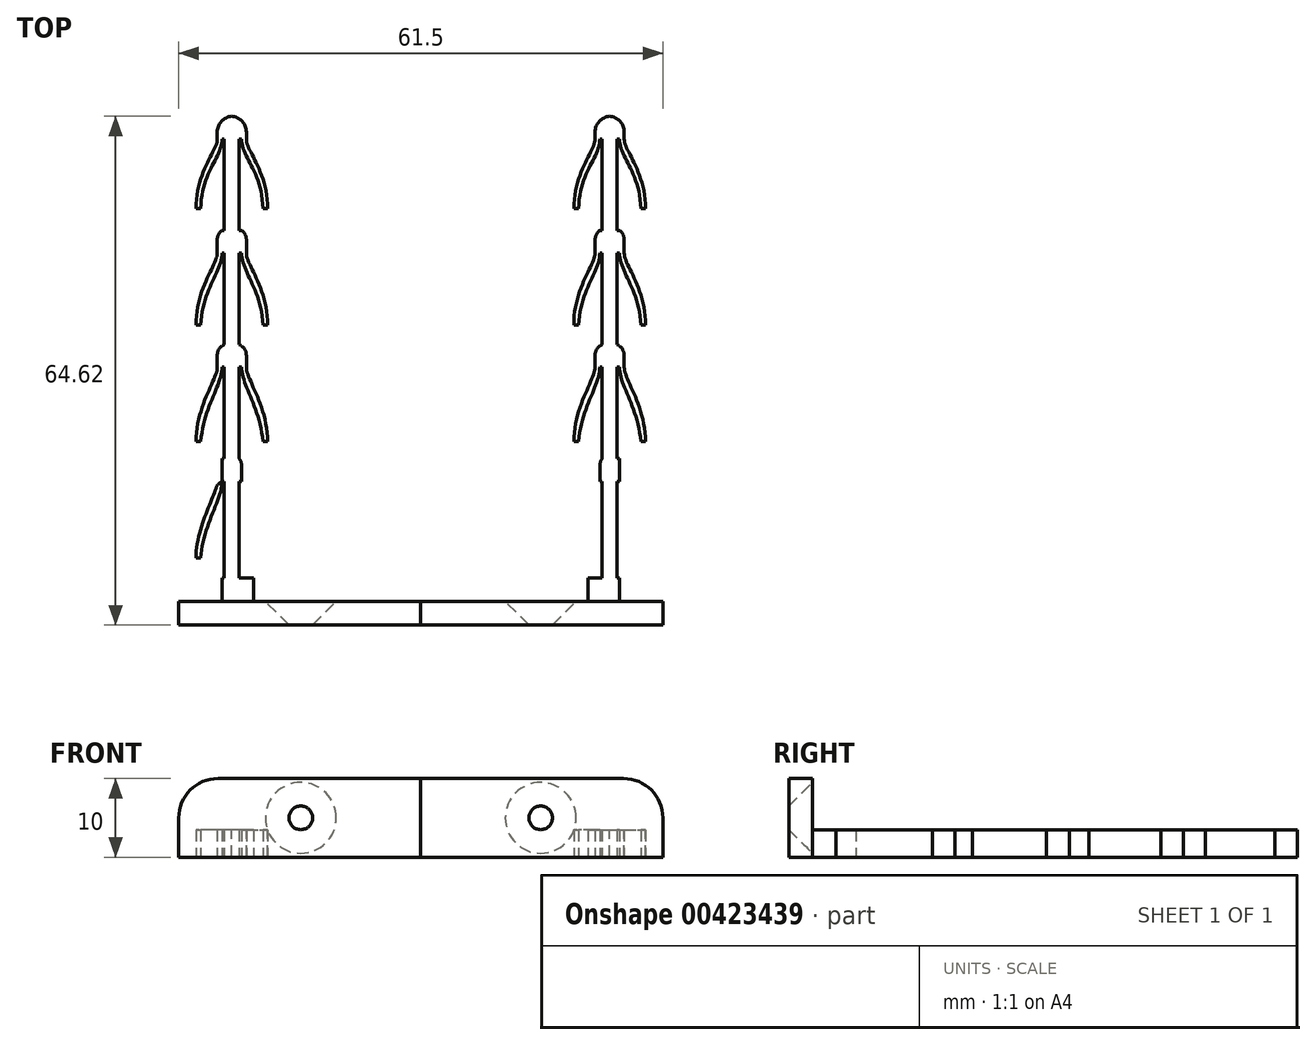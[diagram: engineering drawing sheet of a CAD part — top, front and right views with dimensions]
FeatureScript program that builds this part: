
annotation { "Feature Type Name" : "Feature", "Feature Type Description" : "" }
export const myFeature = defineFeature(function(context is Context, id is Id, definition is map)
    precondition{}
    {
        {
            var Q0;
            Q0=qCreatedBy(makeId("Top.planeOp"),FACE);
            var sketch = newSketch(context, id + "F0", { "sketchPlane" : qUnion([Q0])});
            skLineSegment(sketch, "E0.bottom", {"start": v(0, 0) * mm, "end": v(-15.51, 0) * mm});
            skLineSegment(sketch, "E0.top", {"start": v(0, 3) * mm, "end": v(-15.51, 3) * mm});
            skLineSegment(sketch, "E0.left", {"start": v(0, 0) * mm, "end": v(0, 3) * mm});
            skLineSegment(sketch, "E0.right", {"start": v(-15.51, 0) * mm, "end": v(-15.51, 3) * mm});
            skLineSegment(sketch, "E1.bottom", {"start": v(-10.01, 3) * mm, "end": v(-8.76, 3.02) * mm});
            skLineSegment(sketch, "E1.left", {"start": v(-10.01, 3) * mm, "end": v(-10.01, 18.24) * mm});
            skLineSegment(sketch, "E1.right", {"start": v(-8.76, 3.02) * mm, "end": v(-8.76, 64.62) * mm});
            skLineSegment(sketch, "E2.bottom", {"start": v(-10.01, 3) * mm, "end": v(-11.51, 3) * mm});
            skLineSegment(sketch, "E2.top", {"start": v(-10.01, 6) * mm, "end": v(-11.51, 6) * mm});
            skLineSegment(sketch, "E2.left", {"start": v(-10.01, 3) * mm, "end": v(-10.01, 6) * mm});
            skLineSegment(sketch, "E2.right", {"start": v(-11.51, 3) * mm, "end": v(-11.51, 6) * mm});
            skLineSegment(sketch, "E3.top", {"start": v(-10.01, 18.24) * mm, "end": v(-10.61, 18.24) * mm});
            skLineSegment(sketch, "E4", {"start": v(-13.31, 8.5) * mm, "end": v(-12.71, 8.5) * mm});
            skFitSpline(sketch, "E5", {"points": [v(-10.01, 18.24) * mm, v(-12.71, 8.5) * mm], "startDerivative": vector(0, -7.07) * mm, "endDerivative": vector(-0.68, -12.06) * mm});
            skFitSpline(sketch, "E6", {"points": [v(-10.61, 18.24) * mm, v(-13.31, 8.5) * mm], "startDerivative": vector(0.14, -4.37) * mm, "endDerivative": vector(0.03, -12.59) * mm});
            skLineSegment(sketch, "E7.bottom", {"start": v(-10.61, 18.24) * mm, "end": v(-10.01, 18.24) * mm});
            skLineSegment(sketch, "E7.top", {"start": v(-10.61, 21.13) * mm, "end": v(-10.01, 21.13) * mm});
            skLineSegment(sketch, "E7.left", {"start": v(-10.61, 18.24) * mm, "end": v(-10.61, 21.13) * mm});
            skLineSegment(sketch, "E7.right", {"start": v(-10.01, 18.24) * mm, "end": v(-10.01, 21.13) * mm});
            skLineSegment(sketch, "E8", {"start": v(-10.01, 21.13) * mm, "end": v(-10.01, 64.62) * mm});
            skLineSegment(sketch, "E9", {"start": v(-10.01, 64.62) * mm, "end": v(-8.76, 64.62) * mm});
            skFitSpline(sketch, "E10", {"points": [v(-10.01, 32.74) * mm, v(-12.71, 23.3) * mm], "startDerivative": vector(0, -7.07) * mm, "endDerivative": vector(-1.2, -13.71) * mm});
            skFitSpline(sketch, "E11", {"points": [v(-10.61, 32.74) * mm, v(-13.31, 23.3) * mm], "startDerivative": vector(0.14, -4.37) * mm, "endDerivative": vector(-0.1, -13.84) * mm});
            skLineSegment(sketch, "E12.bottom", {"start": v(-10.61, 32.74) * mm, "end": v(-10.01, 32.74) * mm});
            skLineSegment(sketch, "E12.left", {"start": v(-10.61, 32.74) * mm, "end": v(-10.61, 35.63) * mm});
            skLineSegment(sketch, "E13", {"start": v(-13.31, 23.3) * mm, "end": v(-12.71, 23.3) * mm});
            skLineSegment(sketch, "E14.top", {"start": v(-10.61, 35.63) * mm, "end": v(-10.01, 35.63) * mm});
            skFitSpline(sketch, "E15", {"points": [v(-10.01, 47.24) * mm, v(-12.71, 38.1) * mm], "startDerivative": vector(0, -7.07) * mm, "endDerivative": vector(-0.68, -13.91) * mm});
            skFitSpline(sketch, "E16", {"points": [v(-10.61, 47.24) * mm, v(-13.31, 38.1) * mm], "startDerivative": vector(0.14, -4.37) * mm, "endDerivative": vector(0.16, -14.04) * mm});
            skLineSegment(sketch, "E17.bottom", {"start": v(-10.61, 47.24) * mm, "end": v(-10.01, 47.24) * mm});
            skLineSegment(sketch, "E17.left", {"start": v(-10.61, 47.24) * mm, "end": v(-10.61, 50.13) * mm});
            skLineSegment(sketch, "E18", {"start": v(-13.31, 38.1) * mm, "end": v(-12.71, 38.1) * mm});
            skLineSegment(sketch, "E19.top", {"start": v(-10.61, 50.13) * mm, "end": v(-10.01, 50.13) * mm});
            skFitSpline(sketch, "E20", {"points": [v(-10.01, 61.74) * mm, v(-12.71, 52.9) * mm], "startDerivative": vector(0, -7.07) * mm, "endDerivative": vector(-0.28, -14.05) * mm});
            skFitSpline(sketch, "E21", {"points": [v(-10.61, 61.74) * mm, v(-13.31, 52.9) * mm], "startDerivative": vector(0.14, -4.37) * mm, "endDerivative": vector(0.02, -14.1) * mm});
            skLineSegment(sketch, "E22.bottom", {"start": v(-10.61, 61.74) * mm, "end": v(-10.01, 61.74) * mm});
            skLineSegment(sketch, "E22.left", {"start": v(-10.61, 61.74) * mm, "end": v(-10.61, 64.62) * mm});
            skLineSegment(sketch, "E23", {"start": v(-13.31, 52.9) * mm, "end": v(-12.71, 52.9) * mm});
            skLineSegment(sketch, "E24", {"start": v(-10.61, 64.62) * mm, "end": v(-10.01, 64.62) * mm});
            skLineSegment(sketch, "E25.MirrorCS", {"start": v(-6.91, 18.24) * mm, "end": v(-7.51, 18.24) * mm});
            skLineSegment(sketch, "E26.MirrorCS", {"start": v(-7.51, 18.24) * mm, "end": v(-6.91, 18.24) * mm});
            skLineSegment(sketch, "E27.MirrorCS", {"start": v(-6.91, 32.74) * mm, "end": v(-7.51, 32.74) * mm});
            skLineSegment(sketch, "E28.MirrorCS", {"start": v(-6.91, 47.24) * mm, "end": v(-7.51, 47.24) * mm});
            skLineSegment(sketch, "E29.MirrorCS", {"start": v(-7.51, 6) * mm, "end": v(-6.01, 6) * mm});
            skLineSegment(sketch, "E30.MirrorCS", {"start": v(-6.91, 61.74) * mm, "end": v(-7.51, 61.74) * mm});
            skLineSegment(sketch, "E31.MirrorCS", {"start": v(-6.91, 61.74) * mm, "end": v(-6.91, 64.62) * mm});
            skLineSegment(sketch, "E32.MirrorCS", {"start": v(-6.91, 64.62) * mm, "end": v(-7.51, 64.62) * mm});
            skLineSegment(sketch, "E33.MirrorCS", {"start": v(-4.21, 52.9) * mm, "end": v(-4.81, 52.9) * mm});
            skLineSegment(sketch, "E34.MirrorCS", {"start": v(-4.21, 38.1) * mm, "end": v(-4.81, 38.1) * mm});
            skLineSegment(sketch, "E35.MirrorCS", {"start": v(-4.21, 8.5) * mm, "end": v(-4.81, 8.5) * mm});
            skLineSegment(sketch, "E36.MirrorCS", {"start": v(-6.91, 18.24) * mm, "end": v(-6.91, 21.13) * mm});
            skLineSegment(sketch, "E37.MirrorCS", {"start": v(-4.21, 23.3) * mm, "end": v(-4.81, 23.3) * mm});
            skLineSegment(sketch, "E38.MirrorCS", {"start": v(-7.51, 18.24) * mm, "end": v(-7.51, 21.13) * mm});
            skLineSegment(sketch, "E39.MirrorCS", {"start": v(-6.91, 21.13) * mm, "end": v(-7.51, 21.13) * mm});
            skLineSegment(sketch, "E40.MirrorCS", {"start": v(-6.91, 50.13) * mm, "end": v(-7.51, 50.13) * mm});
            skLineSegment(sketch, "E41.MirrorCS", {"start": v(-6.91, 47.24) * mm, "end": v(-6.91, 50.13) * mm});
            skLineSegment(sketch, "E42.MirrorCS", {"start": v(-6.91, 32.74) * mm, "end": v(-6.91, 35.63) * mm});
            skLineSegment(sketch, "E43.MirrorCS", {"start": v(-6.91, 35.63) * mm, "end": v(-7.51, 35.63) * mm});
            skFitSpline(sketch, "E44.MirrorCS", {"points": [v(-6.91, 61.74) * mm, v(-4.21, 52.9) * mm], "startDerivative": vector(-0.14, -4.37) * mm, "endDerivative": vector(-0.02, -14.1) * mm});
            skLineSegment(sketch, "E45.MirrorCS", {"start": v(-7.51, 21.13) * mm, "end": v(-7.51, 64.62) * mm});
            skFitSpline(sketch, "E46.MirrorCS", {"points": [v(-7.51, 18.24) * mm, v(-4.81, 8.5) * mm], "startDerivative": vector(0, -7.07) * mm, "endDerivative": vector(0.68, -12.06) * mm});
            skFitSpline(sketch, "E47.MirrorCS", {"points": [v(-7.51, 32.74) * mm, v(-4.81, 23.3) * mm], "startDerivative": vector(0, -7.07) * mm, "endDerivative": vector(1.2, -13.71) * mm});
            skFitSpline(sketch, "E48.MirrorCS", {"points": [v(-7.51, 47.24) * mm, v(-4.81, 38.1) * mm], "startDerivative": vector(0, -7.07) * mm, "endDerivative": vector(0.68, -13.91) * mm});
            skFitSpline(sketch, "E49.MirrorCS", {"points": [v(-6.91, 32.74) * mm, v(-4.21, 23.3) * mm], "startDerivative": vector(-0.14, -4.37) * mm, "endDerivative": vector(0.1, -13.84) * mm});
            skFitSpline(sketch, "E50.MirrorCS", {"points": [v(-7.51, 61.74) * mm, v(-4.81, 52.9) * mm], "startDerivative": vector(0, -7.07) * mm, "endDerivative": vector(0.28, -14.05) * mm});
            skFitSpline(sketch, "E51.MirrorCS", {"points": [v(-6.91, 18.24) * mm, v(-4.21, 8.5) * mm], "startDerivative": vector(-0.14, -4.37) * mm, "endDerivative": vector(-0.03, -12.59) * mm});
            skFitSpline(sketch, "E52.MirrorCS", {"points": [v(-6.91, 47.24) * mm, v(-4.21, 38.1) * mm], "startDerivative": vector(-0.14, -4.37) * mm, "endDerivative": vector(-0.16, -14.04) * mm});
            skLineSegment(sketch, "E53.MirrorCS", {"start": v(-7.51, 64.62) * mm, "end": v(-8.76, 64.62) * mm});
            skLineSegment(sketch, "E54.MirrorCS", {"start": v(-7.51, 3) * mm, "end": v(-7.51, 18.24) * mm});
            skLineSegment(sketch, "E55.MirrorCS", {"start": v(-6.01, 3) * mm, "end": v(-6.01, 6) * mm});
            skLineSegment(sketch, "E56.bottom", {"start": v(0, 3) * mm, "end": v(15.24, 3) * mm});
            skLineSegment(sketch, "E56.top", {"start": v(0, 0) * mm, "end": v(15.24, 0) * mm});
            skLineSegment(sketch, "E56.left", {"start": v(0, 3) * mm, "end": v(0, 0) * mm});
            skLineSegment(sketch, "E56.right", {"start": v(15.24, 3) * mm, "end": v(15.24, 0) * mm});
            skLineSegment(sketch, "E57.bottom", {"start": v(-10.01, 61.74) * mm, "end": v(-9.71, 61.74) * mm});
            skLineSegment(sketch, "E57.top", {"start": v(-10.01, 50.13) * mm, "end": v(-9.71, 50.13) * mm});
            skLineSegment(sketch, "E57.left", {"start": v(-10.01, 61.74) * mm, "end": v(-10.01, 50.13) * mm});
            skLineSegment(sketch, "E57.right", {"start": v(-9.71, 61.74) * mm, "end": v(-9.71, 50.13) * mm});
            skLineSegment(sketch, "E58.bottom", {"start": v(-10.01, 47.24) * mm, "end": v(-9.71, 47.24) * mm});
            skLineSegment(sketch, "E58.top", {"start": v(-10.01, 35.63) * mm, "end": v(-9.71, 35.63) * mm});
            skLineSegment(sketch, "E58.left", {"start": v(-10.01, 47.24) * mm, "end": v(-10.01, 35.63) * mm});
            skLineSegment(sketch, "E58.right", {"start": v(-9.71, 47.24) * mm, "end": v(-9.71, 35.63) * mm});
            skLineSegment(sketch, "E59.bottom", {"start": v(-10.01, 32.74) * mm, "end": v(-9.71, 32.74) * mm});
            skLineSegment(sketch, "E59.top", {"start": v(-10.01, 21.13) * mm, "end": v(-9.71, 21.13) * mm});
            skLineSegment(sketch, "E59.left", {"start": v(-10.01, 32.74) * mm, "end": v(-10.01, 21.13) * mm});
            skLineSegment(sketch, "E59.right", {"start": v(-9.71, 32.74) * mm, "end": v(-9.71, 21.13) * mm});
            skLineSegment(sketch, "E60.bottom", {"start": v(-10.01, 18.24) * mm, "end": v(-9.71, 18.24) * mm});
            skLineSegment(sketch, "E60.top", {"start": v(-10.01, 6) * mm, "end": v(-9.71, 6) * mm});
            skLineSegment(sketch, "E60.left", {"start": v(-10.01, 18.24) * mm, "end": v(-10.01, 6) * mm});
            skLineSegment(sketch, "E60.right", {"start": v(-9.71, 18.24) * mm, "end": v(-9.71, 6) * mm});
            skLineSegment(sketch, "E61.MirrorCS", {"start": v(-7.51, 61.74) * mm, "end": v(-7.81, 61.74) * mm});
            skLineSegment(sketch, "E62.MirrorCS", {"start": v(-7.81, 61.74) * mm, "end": v(-7.81, 50.13) * mm});
            skLineSegment(sketch, "E63.MirrorCS", {"start": v(-7.51, 50.13) * mm, "end": v(-7.81, 50.13) * mm});
            skLineSegment(sketch, "E64.MirrorCS", {"start": v(-7.51, 47.24) * mm, "end": v(-7.81, 47.24) * mm});
            skLineSegment(sketch, "E65.MirrorCS", {"start": v(-7.81, 47.24) * mm, "end": v(-7.81, 35.63) * mm});
            skLineSegment(sketch, "E66.MirrorCS", {"start": v(-7.51, 35.63) * mm, "end": v(-7.81, 35.63) * mm});
            skLineSegment(sketch, "E67.MirrorCS", {"start": v(-7.51, 32.74) * mm, "end": v(-7.81, 32.74) * mm});
            skLineSegment(sketch, "E68.MirrorCS", {"start": v(-7.81, 32.74) * mm, "end": v(-7.81, 21.13) * mm});
            skLineSegment(sketch, "E69.MirrorCS", {"start": v(-7.51, 21.13) * mm, "end": v(-7.81, 21.13) * mm});
            skLineSegment(sketch, "E70.MirrorCS", {"start": v(-7.51, 18.24) * mm, "end": v(-7.81, 18.24) * mm});
            skLineSegment(sketch, "E71.MirrorCS", {"start": v(-7.81, 18.24) * mm, "end": v(-7.81, 6) * mm});
            skLineSegment(sketch, "E72.MirrorCS", {"start": v(-7.51, 6) * mm, "end": v(-7.81, 6) * mm});
            skSolve(sketch);
        }
        {
            var Q0;
            {var subQ8=sQuery(id+"F0.wireOp",EDGE,"E1.bottom");Q0=makeQuery(id+"F0.imprint","IMPRINT",FACE,{"disambiguationData":[TD([[makeQuery(id+"F0.imprint","IMPRINT",EDGE,{"derivedFrom":subQ8}),-1.0]])]});}
            var Q1;
            Q1=makeQuery(id+"F0.imprint","IMPRINT",FACE,{"disambiguationData":[TD([[makeQuery(id+"F0.imprint","IMPRINT",EDGE,{"derivedFrom":sQuery(id+"F0.wireOp",EDGE,"E1.bottom")}),1.0]])]});
            var Q2;
            {var subQ2=sQuery(id+"F0.wireOp",EDGE,"E22.bottom");Q2=makeQuery(id+"F0.imprint","IMPRINT",FACE,{"disambiguationData":[TD([[makeQuery(id+"F0.imprint","IMPRINT",EDGE,{"derivedFrom":subQ2}),1.0]])]});}
            var Q3;
            {var subQ0=sQuery(id+"F0.wireOp",EDGE,"E30.MirrorCS");Q3=makeQuery(id+"F0.imprint","IMPRINT",FACE,{"disambiguationData":[TD([[makeQuery(id+"F0.imprint","IMPRINT",EDGE,{"derivedFrom":subQ0}),-1.0]])]});}
            var Q4;
            Q4=makeQuery(id+"F0.imprint","IMPRINT",FACE,{"disambiguationData":[TD([[makeQuery(id+"F0.imprint","IMPRINT",EDGE,{"derivedFrom":sQuery(id+"F0.wireOp",EDGE,"E30.MirrorCS")}),1.0]])]});
            var Q5;
            Q5=makeQuery(id+"F0.imprint","IMPRINT",FACE,{"disambiguationData":[TD([[makeQuery(id+"F0.imprint","IMPRINT",EDGE,{"derivedFrom":sQuery(id+"F0.wireOp",EDGE,"E20")}),-1.0]])]});
            var Q6;
            {var subQ0=sQuery(id+"F0.wireOp",EDGE,"E17.bottom");Q6=makeQuery(id+"F0.imprint","IMPRINT",FACE,{"disambiguationData":[TD([[makeQuery(id+"F0.imprint","IMPRINT",EDGE,{"derivedFrom":subQ0}),1.0]])]});}
            var Q7;
            {var subQ0=sQuery(id+"F0.wireOp",EDGE,"E28.MirrorCS");Q7=makeQuery(id+"F0.imprint","IMPRINT",FACE,{"disambiguationData":[TD([[makeQuery(id+"F0.imprint","IMPRINT",EDGE,{"derivedFrom":subQ0}),-1.0]])]});}
            var Q8;
            Q8=makeQuery(id+"F0.imprint","IMPRINT",FACE,{"disambiguationData":[TD([[makeQuery(id+"F0.imprint","IMPRINT",EDGE,{"derivedFrom":sQuery(id+"F0.wireOp",EDGE,"E28.MirrorCS")}),1.0]])]});
            var Q9;
            Q9=makeQuery(id+"F0.imprint","IMPRINT",FACE,{"disambiguationData":[TD([[makeQuery(id+"F0.imprint","IMPRINT",EDGE,{"derivedFrom":sQuery(id+"F0.wireOp",EDGE,"E15")}),-1.0]])]});
            var Q10;
            {var subQ0=sQuery(id+"F0.wireOp",EDGE,"E12.bottom");Q10=makeQuery(id+"F0.imprint","IMPRINT",FACE,{"disambiguationData":[TD([[makeQuery(id+"F0.imprint","IMPRINT",EDGE,{"derivedFrom":subQ0}),1.0]])]});}
            var Q11;
            {var subQ0=sQuery(id+"F0.wireOp",EDGE,"E27.MirrorCS");Q11=makeQuery(id+"F0.imprint","IMPRINT",FACE,{"disambiguationData":[TD([[makeQuery(id+"F0.imprint","IMPRINT",EDGE,{"derivedFrom":subQ0}),-1.0]])]});}
            var Q12;
            Q12=makeQuery(id+"F0.imprint","IMPRINT",FACE,{"disambiguationData":[TD([[makeQuery(id+"F0.imprint","IMPRINT",EDGE,{"derivedFrom":sQuery(id+"F0.wireOp",EDGE,"E27.MirrorCS")}),1.0]])]});
            var Q13;
            Q13=makeQuery(id+"F0.imprint","IMPRINT",FACE,{"disambiguationData":[TD([[makeQuery(id+"F0.imprint","IMPRINT",EDGE,{"derivedFrom":sQuery(id+"F0.wireOp",EDGE,"E10")}),-1.0]])]});
            var Q14;
            Q14=makeQuery(id+"F0.imprint","IMPRINT",FACE,{"disambiguationData":[TD([[makeQuery(id+"F0.imprint","IMPRINT",EDGE,{"derivedFrom":sQuery(id+"F0.wireOp",EDGE,"E26.MirrorCS")}),1.0]])]});
            var Q15;
            Q15=makeQuery(id+"F0.imprint","IMPRINT",FACE,{"disambiguationData":[TD([[makeQuery(id+"F0.imprint","IMPRINT",EDGE,{"derivedFrom":sQuery(id+"F0.wireOp",EDGE,"E7.bottom")}),1.0]])]});
            var Q16;
            Q16=makeQuery(id+"F0.imprint","IMPRINT",FACE,{"disambiguationData":[TD([[makeQuery(id+"F0.imprint","IMPRINT",EDGE,{"derivedFrom":sQuery(id+"F0.wireOp",EDGE,"E4")}),1.0]])]});
            var Q17;
            Q17=makeQuery(id+"F0.imprint","IMPRINT",FACE,{"disambiguationData":[TD([[makeQuery(id+"F0.imprint","IMPRINT",EDGE,{"derivedFrom":sQuery(id+"F0.wireOp",EDGE,"E26.MirrorCS")}),-1.0]])]});
            var Q18;
            {var subQ4=sQuery(id+"F0.wireOp",EDGE,"E29.MirrorCS");Q18=makeQuery(id+"F0.imprint","IMPRINT",FACE,{"disambiguationData":[TD([[makeQuery(id+"F0.imprint","IMPRINT",EDGE,{"derivedFrom":subQ4}),-1.0]])]});}
            var Q19;
            Q19=makeQuery(id+"F0.imprint","IMPRINT",FACE,{"disambiguationData":[TD([[makeQuery(id+"F0.imprint","IMPRINT",EDGE,{"derivedFrom":sQuery(id+"F0.wireOp",EDGE,"E2.bottom")}),-1.0]])]});
            extrude(context, id + "F1", {"entities" : qUnion([Q0, Q1, Q2, Q3, Q4, Q5, Q6, Q7, Q8, Q9, Q10, Q11, Q12, Q13, Q14, Q15, Q16, Q17, Q18, Q19]), "depth" : 3.5 * mm});
        }
        {
            var Q0;
            Q0=makeQuery(id+"F0.imprint","IMPRINT",FACE,{"disambiguationData":[TD([[makeQuery(id+"F0.imprint","IMPRINT",EDGE,{"derivedFrom":sQuery(id+"F0.wireOp",EDGE,"E0.bottom")}),-1.0]])]});
            var Q1;
            Q1=makeQuery(id+"F0.imprint","IMPRINT",FACE,{"disambiguationData":[TD([[makeQuery(id+"F0.imprint","IMPRINT",EDGE,{"derivedFrom":sQuery(id+"F0.wireOp",EDGE,"E56.bottom")}),-1.0]])]});
            extrude(context, id + "F2", {"entities" : qUnion([Q0, Q1]), "operationType" : NewBodyOperationType.ADD, "depth" : 10 * mm});
        }
        {
            var Q0;
            Q0=makeQuery(id+"F2.opExtrude","CAP_EDGE",EDGE,{"disambiguationData":[OSD([sQuery(id+"F0.wireOp",EDGE,"E0.right")])],"isStart":false});
            fillet(context, id + "F3", {"entities" : qUnion([Q0]), "radius" : 5 * mm, "tangentPropagation" : true, "allowEdgeOverflow" : false});
        }
        {
            var Q0;
            Q0=makeQuery(id+"F1.opExtrude","SWEPT_EDGE",EDGE,{"disambiguationData":[OSD([sQuery(id+"F0.wireOp",EDGE,"E22.left"),sQuery(id+"F0.wireOp",EDGE,"E24")])]});
            var Q1;
            Q1=makeQuery(id+"F1.opExtrude","SWEPT_EDGE",EDGE,{"disambiguationData":[OSD([sQuery(id+"F0.wireOp",EDGE,"E31.MirrorCS"),sQuery(id+"F0.wireOp",EDGE,"E32.MirrorCS")])]});
            fillet(context, id + "F4", {"entities" : qUnion([Q0, Q1]), "radius" : 2 * mm, "tangentPropagation" : true, "allowEdgeOverflow" : false});
        }
        {
            var Q0;
            Q0=qCreatedBy(makeId("Front.planeOp"),FACE);
            var sketch = newSketch(context, id + "F5", { "sketchPlane" : qUnion([Q0])});
            skLineSegment(sketch, "E73", {"start": v(0, 0) * mm, "end": v(0, 10) * mm});
            skCircle(sketch, "E74", {"center": v(0, 5) * mm, "radius": 1.5 * mm});
            skSolve(sketch);
        }
        {
            var Q0;
            {var subQ0=sQuery(id+"F5.wireOp",EDGE,"E74");var subQ1=sQuery(id+"F5.wireOp",EDGE,"E73");var subQ2=makeQuery(id+"F5.imprint","INTERSECT",VERTEX,{"disambiguationData":[OD(0.0)],"derivedFrom":[subQ1,subQ0]});Q0=makeQuery(id+"F5.imprint","IMPRINT",FACE,{"disambiguationData":[TD([[makeQuery(id+"F5.imprint","IMPRINT",EDGE,{"disambiguationData":[TD([[subQ2,-1.0]])],"derivedFrom":subQ1}),1.0]])]});}
            var Q1;
            {var subQ0=sQuery(id+"F5.wireOp",EDGE,"E74");var subQ1=sQuery(id+"F5.wireOp",EDGE,"E73");var subQ2=makeQuery(id+"F5.imprint","INTERSECT",VERTEX,{"disambiguationData":[OD(0.0)],"derivedFrom":[subQ1,subQ0]});Q1=makeQuery(id+"F5.imprint","IMPRINT",FACE,{"disambiguationData":[TD([[makeQuery(id+"F5.imprint","IMPRINT",EDGE,{"disambiguationData":[TD([[subQ2,-1.0]])],"derivedFrom":subQ1}),-1.0]])]});}
            extrude(context, id + "F6", {"entities" : qUnion([Q0, Q1]), "operationType" : NewBodyOperationType.REMOVE, "oppositeDirection" : true, "depth" : 25 * mm});
        }
        {
            var Q0;
            Q0=makeQuery(id+"F6.boolean.opBoolean","INTERSECT",EDGE,{"derivedFrom":[makeQuery(id+"F2.opExtrude","SWEPT_FACE",FACE,{"disambiguationData":[OSD([sQuery(id+"F0.wireOp",EDGE,"E0.top"),sQuery(id+"F0.wireOp",EDGE,"E2.bottom"),sQuery(id+"F0.wireOp",EDGE,"E56.bottom")])]}),makeQuery(id+"F6.opExtrude","SWEPT_FACE",FACE,{"disambiguationData":[OSD([sQuery(id+"F5.wireOp",EDGE,"E74")])]})]});
            chamfer(context, id + "F7", {"entities" : qUnion([Q0]), "width" : 3 * mm, "tangentPropagation" : true});
        }
        {
            var Q0;
            Q0=makeQuery(id+"F1.opExtrude","SWEPT_EDGE",EDGE,{"disambiguationData":[OSD([sQuery(id+"F0.wireOp",EDGE,"E36.MirrorCS"),sQuery(id+"F0.wireOp",EDGE,"E39.MirrorCS")])]});
            var Q1;
            Q1=makeQuery(id+"F1.opExtrude","SWEPT_EDGE",EDGE,{"disambiguationData":[OSD([sQuery(id+"F0.wireOp",EDGE,"E7.top"),sQuery(id+"F0.wireOp",EDGE,"E7.left")])]});
            var Q2;
            Q2=makeQuery(id+"F1.opExtrude","SWEPT_EDGE",EDGE,{"disambiguationData":[OSD([sQuery(id+"F0.wireOp",EDGE,"E12.left"),sQuery(id+"F0.wireOp",EDGE,"E14.top")])]});
            var Q3;
            Q3=makeQuery(id+"F1.opExtrude","SWEPT_EDGE",EDGE,{"disambiguationData":[OSD([sQuery(id+"F0.wireOp",EDGE,"E42.MirrorCS"),sQuery(id+"F0.wireOp",EDGE,"E43.MirrorCS")])]});
            var Q4;
            Q4=makeQuery(id+"F1.opExtrude","SWEPT_EDGE",EDGE,{"disambiguationData":[OSD([sQuery(id+"F0.wireOp",EDGE,"E40.MirrorCS"),sQuery(id+"F0.wireOp",EDGE,"E41.MirrorCS")])]});
            var Q5;
            Q5=makeQuery(id+"F1.opExtrude","SWEPT_EDGE",EDGE,{"disambiguationData":[OSD([sQuery(id+"F0.wireOp",EDGE,"E17.left"),sQuery(id+"F0.wireOp",EDGE,"E19.top")])]});
            fillet(context, id + "F8", {"entities" : qUnion([Q0, Q1, Q2, Q3, Q4, Q5]), "radius" : 1.5 * mm, "tangentPropagation" : true, "allowEdgeOverflow" : false});
        }
        {
            var Q0;
            Q0=makeQuery(id+"F1.opExtrude","SWEPT_BODY",BODY,{"disambiguationData":[OSD([sQuery(id+"F0.wireOp",EDGE,"E0.top"),sQuery(id+"F0.wireOp",EDGE,"E1.left"),sQuery(id+"F0.wireOp",EDGE,"E2.bottom"),sQuery(id+"F0.wireOp",EDGE,"E2.top"),sQuery(id+"F0.wireOp",EDGE,"E2.right"),sQuery(id+"F0.wireOp",EDGE,"E4"),sQuery(id+"F0.wireOp",EDGE,"E5"),sQuery(id+"F0.wireOp",EDGE,"E6"),sQuery(id+"F0.wireOp",EDGE,"E7.top"),sQuery(id+"F0.wireOp",EDGE,"E7.left"),sQuery(id+"F0.wireOp",EDGE,"E8"),sQuery(id+"F0.wireOp",EDGE,"E9"),sQuery(id+"F0.wireOp",EDGE,"E10"),sQuery(id+"F0.wireOp",EDGE,"E11"),sQuery(id+"F0.wireOp",EDGE,"E12.left"),sQuery(id+"F0.wireOp",EDGE,"E13"),sQuery(id+"F0.wireOp",EDGE,"E14.top"),sQuery(id+"F0.wireOp",EDGE,"E15"),sQuery(id+"F0.wireOp",EDGE,"E16"),sQuery(id+"F0.wireOp",EDGE,"E17.left"),sQuery(id+"F0.wireOp",EDGE,"E18"),sQuery(id+"F0.wireOp",EDGE,"E19.top"),sQuery(id+"F0.wireOp",EDGE,"E20"),sQuery(id+"F0.wireOp",EDGE,"E21"),sQuery(id+"F0.wireOp",EDGE,"E22.left"),sQuery(id+"F0.wireOp",EDGE,"E23"),sQuery(id+"F0.wireOp",EDGE,"E24"),sQuery(id+"F0.wireOp",EDGE,"E29.MirrorCS"),sQuery(id+"F0.wireOp",EDGE,"E31.MirrorCS"),sQuery(id+"F0.wireOp",EDGE,"E32.MirrorCS"),sQuery(id+"F0.wireOp",EDGE,"E33.MirrorCS"),sQuery(id+"F0.wireOp",EDGE,"E34.MirrorCS"),sQuery(id+"F0.wireOp",EDGE,"E35.MirrorCS"),sQuery(id+"F0.wireOp",EDGE,"E36.MirrorCS"),sQuery(id+"F0.wireOp",EDGE,"E37.MirrorCS"),sQuery(id+"F0.wireOp",EDGE,"E39.MirrorCS"),sQuery(id+"F0.wireOp",EDGE,"E40.MirrorCS"),sQuery(id+"F0.wireOp",EDGE,"E41.MirrorCS"),sQuery(id+"F0.wireOp",EDGE,"E42.MirrorCS"),sQuery(id+"F0.wireOp",EDGE,"E43.MirrorCS"),sQuery(id+"F0.wireOp",EDGE,"E44.MirrorCS"),sQuery(id+"F0.wireOp",EDGE,"E45.MirrorCS"),sQuery(id+"F0.wireOp",EDGE,"E46.MirrorCS"),sQuery(id+"F0.wireOp",EDGE,"E47.MirrorCS"),sQuery(id+"F0.wireOp",EDGE,"E48.MirrorCS"),sQuery(id+"F0.wireOp",EDGE,"E49.MirrorCS"),sQuery(id+"F0.wireOp",EDGE,"E50.MirrorCS"),sQuery(id+"F0.wireOp",EDGE,"E51.MirrorCS"),sQuery(id+"F0.wireOp",EDGE,"E52.MirrorCS"),sQuery(id+"F0.wireOp",EDGE,"E53.MirrorCS"),sQuery(id+"F0.wireOp",EDGE,"E54.MirrorCS"),sQuery(id+"F0.wireOp",EDGE,"E55.MirrorCS")])]});
            var Q1;
            Q1=makeQuery(id+"F2.opExtrude","SWEPT_FACE",FACE,{"disambiguationData":[OSD([sQuery(id+"F0.wireOp",EDGE,"E56.right")])]});
            mirror(context, id + "F9", {"operationType" : NewBodyOperationType.ADD, "entities" : qUnion([Q0]), "mirrorPlane" : qUnion([Q1])});
        }
    });
